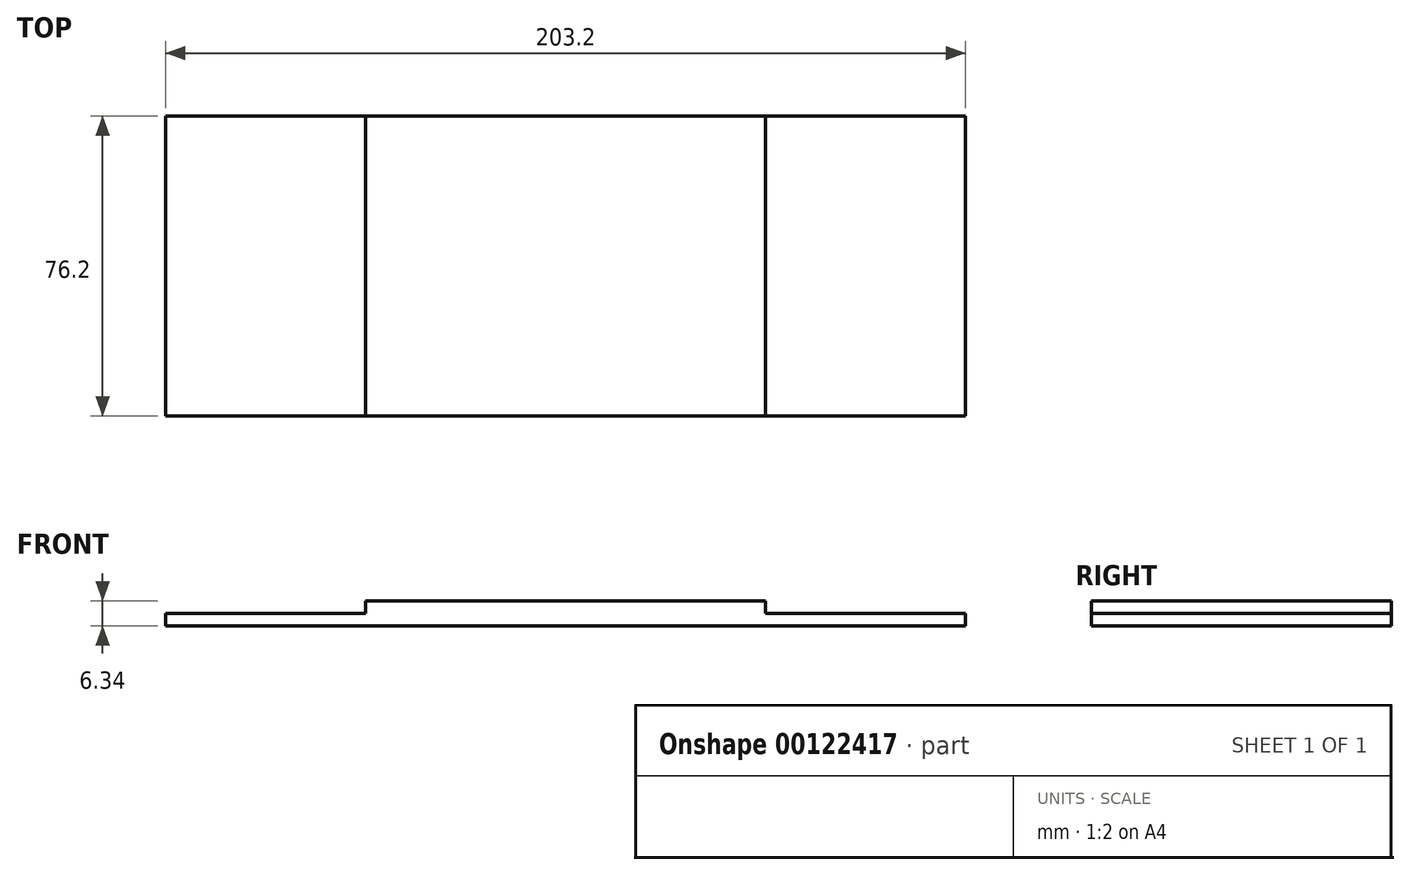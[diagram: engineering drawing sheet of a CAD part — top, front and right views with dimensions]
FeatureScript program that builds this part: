
annotation { "Feature Type Name" : "Feature", "Feature Type Description" : "" }
export const myFeature = defineFeature(function(context is Context, id is Id, definition is map)
    precondition{}
    {
        {
            var Q0;
            Q0=qCreatedBy(makeId("Front.planeOp"),FACE);
            var sketch = newSketch(context, id + "F0", { "sketchPlane" : qUnion([Q0])});
            skLineSegment(sketch, "E0.bottom", {"start": v(50.8, 3.18) * mm, "end": v(-50.8, 3.18) * mm});
            skLineSegment(sketch, "E0.top", {"start": v(50.8, -3.18) * mm, "end": v(-50.8, -3.18) * mm});
            skLineSegment(sketch, "E0.left", {"start": v(50.8, 3.18) * mm, "end": v(50.8, -3.18) * mm});
            skLineSegment(sketch, "E0.right", {"start": v(-50.8, 3.18) * mm, "end": v(-50.8, -3.18) * mm});
            skPoint(sketch, "E0.middle", {"position": v(0, 0) * mm});
            skPoint(sketch, "E1.oppositeSnap0", {"position": v(-50.8, 0) * mm});
            skLineSegment(sketch, "E1.bottom", {"start": v(-50.8, -3.18) * mm, "end": v(-101.6, -3.18) * mm});
            skLineSegment(sketch, "E1.top", {"start": v(-50.8, 0) * mm, "end": v(-101.6, 0) * mm});
            skLineSegment(sketch, "E1.left", {"start": v(-50.8, -3.18) * mm, "end": v(-50.8, 0) * mm});
            skLineSegment(sketch, "E1.right", {"start": v(-101.6, -3.18) * mm, "end": v(-101.6, 0) * mm});
            skPoint(sketch, "E2.oppositeSnap0", {"position": v(50.8, 0) * mm});
            skLineSegment(sketch, "E2.bottom", {"start": v(50.8, -3.18) * mm, "end": v(101.6, -3.18) * mm});
            skLineSegment(sketch, "E2.top", {"start": v(50.8, 0) * mm, "end": v(101.6, 0) * mm});
            skLineSegment(sketch, "E2.left", {"start": v(50.8, -3.18) * mm, "end": v(50.8, 0) * mm});
            skLineSegment(sketch, "E2.right", {"start": v(101.6, -3.17) * mm, "end": v(101.6, 0) * mm});
            skSolve(sketch);
        }
        {
            var Q0;
            {var subQ1=sQuery(id+"F0.wireOp",EDGE,"E0.bottom");var subQ4=sQuery(id+"F0.wireOp",EDGE,"E2.bottom");var subQ7=sQuery(id+"F0.wireOp",EDGE,"E1.bottom");Q0=qUnion([makeQuery(id+"F0.imprint","IMPRINT",FACE,{"disambiguationData":[TD([[makeQuery(id+"F0.imprint","IMPRINT",EDGE,{"derivedFrom":subQ4}),1.0]])]}),makeQuery(id+"F0.imprint","IMPRINT",FACE,{"disambiguationData":[TD([[makeQuery(id+"F0.imprint","IMPRINT",EDGE,{"derivedFrom":subQ7}),-1.0]])]}),makeQuery(id+"F0.imprint","IMPRINT",FACE,{"disambiguationData":[TD([[makeQuery(id+"F0.imprint","IMPRINT",EDGE,{"derivedFrom":subQ1}),1.0]])]})]);}
            extrude(context, id + "F1", {"entities" : qUnion([Q0]), "depth" : 76.2 * mm});
        }
    });
